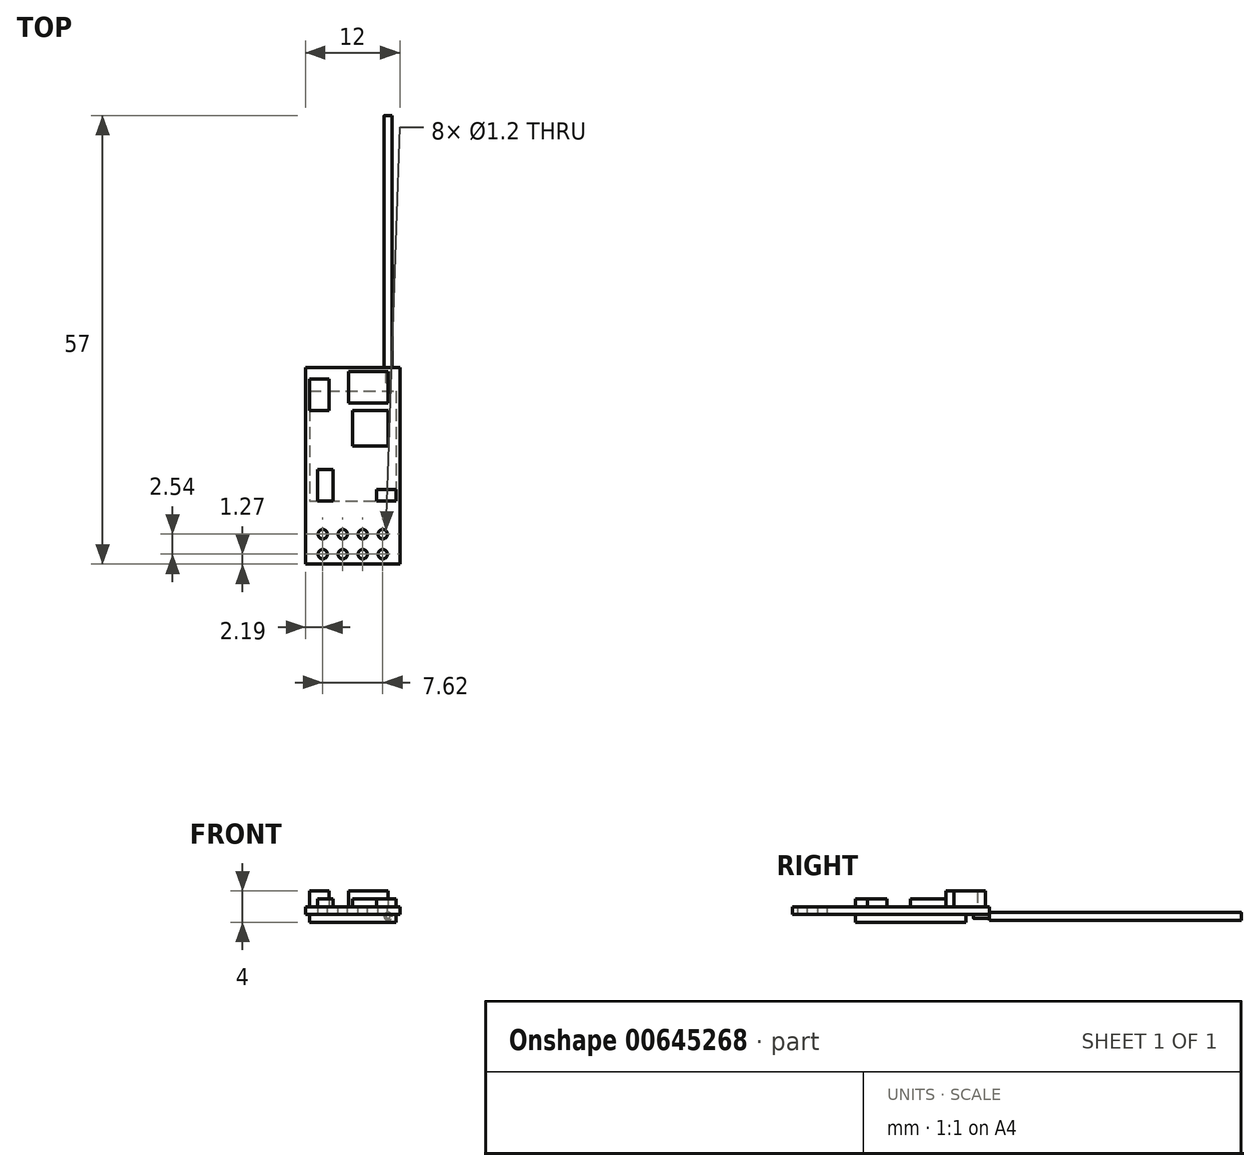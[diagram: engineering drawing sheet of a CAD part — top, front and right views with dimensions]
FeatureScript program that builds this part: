
annotation { "Feature Type Name" : "Feature", "Feature Type Description" : "" }
export const myFeature = defineFeature(function(context is Context, id is Id, definition is map)
    precondition{}
    {
        {
            var Q0;
            Q0=qCreatedBy(makeId("Top.planeOp"),FACE);
            var sketch = newSketch(context, id + "F0", { "sketchPlane" : qUnion([Q0])});
            skLineSegment(sketch, "E0.bottom", {"start": v(6, 0) * mm, "end": v(-6, 0) * mm});
            skLineSegment(sketch, "E0.top", {"start": v(6, 25) * mm, "end": v(-6, 25) * mm});
            skLineSegment(sketch, "E0.left", {"start": v(6, 0) * mm, "end": v(6, 25) * mm});
            skLineSegment(sketch, "E0.right", {"start": v(-6, 0) * mm, "end": v(-6, 25) * mm});
            skPoint(sketch, "E0.middle", {"position": v(0, 12.5) * mm});
            skCircle(sketch, "E1", {"center": v(3.81, 1.27) * mm, "radius": 0.6 * mm});
            skCircle(sketch, "E2.0.1.0", {"center": v(3.81, 3.81) * mm, "radius": 0.6 * mm});
            skCircle(sketch, "E2.1.0.0", {"center": v(1.27, 1.27) * mm, "radius": 0.6 * mm});
            skCircle(sketch, "E2.1.1.0", {"center": v(1.27, 3.81) * mm, "radius": 0.6 * mm});
            skCircle(sketch, "E2.2.0.0", {"center": v(-1.27, 1.27) * mm, "radius": 0.6 * mm});
            skCircle(sketch, "E2.2.1.0", {"center": v(-1.27, 3.81) * mm, "radius": 0.6 * mm});
            skCircle(sketch, "E2.3.0.0", {"center": v(-3.81, 1.27) * mm, "radius": 0.6 * mm});
            skCircle(sketch, "E2.3.1.0", {"center": v(-3.81, 3.81) * mm, "radius": 0.6 * mm});
            skLineSegment(sketch, "E2.direction1", {"start": v(3.81, 1.27) * mm, "end": v(1.27, 1.27) * mm, "construction": true});
            skLineSegment(sketch, "E2.direction2", {"start": v(3.81, 1.27) * mm, "end": v(3.81, 3.81) * mm, "construction": true});
            skSolve(sketch);
        }
        {
            var Q0;
            Q0=qCreatedBy(makeId("Top.planeOp"),FACE);
            var sketch = newSketch(context, id + "F1", { "sketchPlane" : qUnion([Q0])});
            skLineSegment(sketch, "E3.bottom", {"start": v(0, 19.5) * mm, "end": v(4.5, 19.5) * mm});
            skLineSegment(sketch, "E3.top", {"start": v(0, 15) * mm, "end": v(4.5, 15) * mm});
            skLineSegment(sketch, "E3.left", {"start": v(0, 19.5) * mm, "end": v(0, 15) * mm});
            skLineSegment(sketch, "E3.right", {"start": v(4.5, 19.5) * mm, "end": v(4.5, 15) * mm});
            skLineSegment(sketch, "E4.bottom", {"start": v(-0.5, 24.5) * mm, "end": v(4.5, 24.5) * mm});
            skLineSegment(sketch, "E4.top", {"start": v(-0.5, 20.5) * mm, "end": v(4.5, 20.5) * mm});
            skLineSegment(sketch, "E4.left", {"start": v(-0.5, 24.5) * mm, "end": v(-0.5, 20.5) * mm});
            skLineSegment(sketch, "E4.right", {"start": v(4.5, 24.5) * mm, "end": v(4.5, 20.5) * mm});
            skLineSegment(sketch, "E5.bottom", {"start": v(-5.5, 23.5) * mm, "end": v(-3, 23.5) * mm});
            skLineSegment(sketch, "E5.top", {"start": v(-5.5, 19.5) * mm, "end": v(-3, 19.5) * mm});
            skLineSegment(sketch, "E5.left", {"start": v(-5.5, 23.5) * mm, "end": v(-5.5, 19.5) * mm});
            skLineSegment(sketch, "E5.right", {"start": v(-3, 23.5) * mm, "end": v(-3, 19.5) * mm});
            skLineSegment(sketch, "E6.bottom", {"start": v(-4.5, 12) * mm, "end": v(-2.5, 12) * mm});
            skLineSegment(sketch, "E6.top", {"start": v(-4.5, 8) * mm, "end": v(-2.5, 8) * mm});
            skLineSegment(sketch, "E6.left", {"start": v(-4.5, 12) * mm, "end": v(-4.5, 8) * mm});
            skLineSegment(sketch, "E6.right", {"start": v(-2.5, 12) * mm, "end": v(-2.5, 8) * mm});
            skLineSegment(sketch, "E7.bottom", {"start": v(3, 9.5) * mm, "end": v(5.5, 9.5) * mm});
            skLineSegment(sketch, "E7.top", {"start": v(3, 8) * mm, "end": v(5.5, 8) * mm});
            skLineSegment(sketch, "E7.left", {"start": v(3, 9.5) * mm, "end": v(3, 8) * mm});
            skLineSegment(sketch, "E7.right", {"start": v(5.5, 9.5) * mm, "end": v(5.5, 8) * mm});
            skSolve(sketch);
        }
        {
            var Q0;
            Q0 = qSketchRegion(id + "F0", true);
            extrude(context, id + "F2", {"entities" : qUnion([Q0]), "oppositeDirection" : true, "depth" : 1 * mm, "offsetDistance" : 25 * mm});
        }
        {
            var Q0;
            Q0=makeQuery(id+"F1.imprint","IMPRINT",FACE,{"disambiguationData":[TD([[makeQuery(id+"F1.imprint","IMPRINT",EDGE,{"derivedFrom":sQuery(id+"F1.wireOp",EDGE,"E3.bottom")}),-1.0]])]});
            var Q1;
            Q1=makeQuery(id+"F1.imprint","IMPRINT",FACE,{"disambiguationData":[TD([[makeQuery(id+"F1.imprint","IMPRINT",EDGE,{"derivedFrom":sQuery(id+"F1.wireOp",EDGE,"E6.bottom")}),-1.0]])]});
            var Q2;
            Q2=makeQuery(id+"F1.imprint","IMPRINT",FACE,{"disambiguationData":[TD([[makeQuery(id+"F1.imprint","IMPRINT",EDGE,{"derivedFrom":sQuery(id+"F1.wireOp",EDGE,"E7.bottom")}),-1.0]])]});
            extrude(context, id + "F3", {"entities" : qUnion([Q0, Q1, Q2]), "depth" : 1 * mm, "offsetDistance" : 25 * mm});
        }
        {
            var Q0;
            Q0=makeQuery(id+"F1.imprint","IMPRINT",FACE,{"disambiguationData":[TD([[makeQuery(id+"F1.imprint","IMPRINT",EDGE,{"derivedFrom":sQuery(id+"F1.wireOp",EDGE,"E4.bottom")}),-1.0]])]});
            var Q1;
            Q1=makeQuery(id+"F1.imprint","IMPRINT",FACE,{"disambiguationData":[TD([[makeQuery(id+"F1.imprint","IMPRINT",EDGE,{"derivedFrom":sQuery(id+"F1.wireOp",EDGE,"E5.bottom")}),-1.0]])]});
            extrude(context, id + "F4", {"entities" : qUnion([Q0, Q1]), "depth" : 2 * mm, "offsetDistance" : 25 * mm});
        }
        {
            var Q0;
            Q0=makeQuery(id+"F2.opExtrude","CAP_FACE",FACE,{"disambiguationData":[OSD([sQuery(id+"F0.wireOp",EDGE,"E0.bottom"),sQuery(id+"F0.wireOp",EDGE,"E0.top"),sQuery(id+"F0.wireOp",EDGE,"E0.left"),sQuery(id+"F0.wireOp",EDGE,"E0.right"),sQuery(id+"F0.wireOp",EDGE,"E1"),sQuery(id+"F0.wireOp",EDGE,"E2.0.1.0"),sQuery(id+"F0.wireOp",EDGE,"E2.1.0.0"),sQuery(id+"F0.wireOp",EDGE,"E2.1.1.0"),sQuery(id+"F0.wireOp",EDGE,"E2.2.0.0"),sQuery(id+"F0.wireOp",EDGE,"E2.2.1.0"),sQuery(id+"F0.wireOp",EDGE,"E2.3.0.0"),sQuery(id+"F0.wireOp",EDGE,"E2.3.1.0")])],"isStart":false});
            var sketch = newSketch(context, id + "F5", { "sketchPlane" : qUnion([Q0])});
            skLineSegment(sketch, "E8.bottom", {"start": v(-5.5, -22) * mm, "end": v(5.5, -22) * mm});
            skLineSegment(sketch, "E8.top", {"start": v(-5.5, -8) * mm, "end": v(5.5, -8) * mm});
            skLineSegment(sketch, "E8.left", {"start": v(-5.5, -22) * mm, "end": v(-5.5, -8) * mm});
            skLineSegment(sketch, "E8.right", {"start": v(5.5, -22) * mm, "end": v(5.5, -8) * mm});
            skPoint(sketch, "E8.middle", {"position": v(0, -15) * mm});
            skLineSegment(sketch, "E9.top", {"start": v(4.75, -56) * mm, "end": v(3.75, -56) * mm});
            skSolve(sketch);
        }
        {
            var Q0;
            Q0=makeQuery(id+"F5.imprint","IMPRINT",FACE,{"disambiguationData":[TD([[makeQuery(id+"F5.imprint","IMPRINT",EDGE,{"derivedFrom":sQuery(id+"F5.wireOp",EDGE,"E8.bottom")}),1.0]])]});
            extrude(context, id + "F6", {"entities" : qUnion([Q0]), "operationType" : NewBodyOperationType.ADD, "depth" : 1 * mm, "offsetDistance" : 25 * mm});
        }
        {
            var Q0;
            Q0=makeQuery(id+"F2.opExtrude","SWEPT_FACE",FACE,{"disambiguationData":[OSD([sQuery(id+"F0.wireOp",EDGE,"E0.top")])]});
            var sketch = newSketch(context, id + "F7", { "sketchPlane" : qUnion([Q0])});
            skArc(sketch, "E10", {"start": v(-4.75, -1.25) * mm, "mid": v(-4.5, -1.5) * mm, "end": v(-4.25, -1.25) * mm});
            skCircle(sketch, "E11", {"center": v(-4.5, -1.25) * mm, "radius": 0.5 * mm});
            skLineSegment(sketch, "E12", {"start": v(-4.25, -1.25) * mm, "end": v(-4.25, -1) * mm});
            skLineSegment(sketch, "E13", {"start": v(-4.75, -1.25) * mm, "end": v(-4.75, -1) * mm});
            skSolve(sketch);
        }
        {
            var Q0;
            Q0 = qSketchRegion(id + "F7", true);
            var Q1;
            Q1=makeQuery(id+"F7.imprint","IMPRINT",FACE,{"disambiguationData":[TD([[makeQuery(id+"F7.imprint","IMPRINT",EDGE,{"derivedFrom":sQuery(id+"F7.wireOp",EDGE,"E10")}),1.0]])]});
            extrude(context, id + "F8", {"entities" : qUnion([Q0, Q1]), "depth" : 32 * mm, "offsetDistance" : 25 * mm});
        }
        {
            var Q0;
            Q0=makeQuery(id+"F7.imprint","IMPRINT",FACE,{"disambiguationData":[TD([[makeQuery(id+"F7.imprint","IMPRINT",EDGE,{"derivedFrom":sQuery(id+"F7.wireOp",EDGE,"E10")}),1.0]])]});
            extrude(context, id + "F9", {"entities" : qUnion([Q0]), "operationType" : NewBodyOperationType.ADD, "oppositeDirection" : true, "depth" : 2 * mm, "offsetDistance" : 25 * mm});
        }
    });
